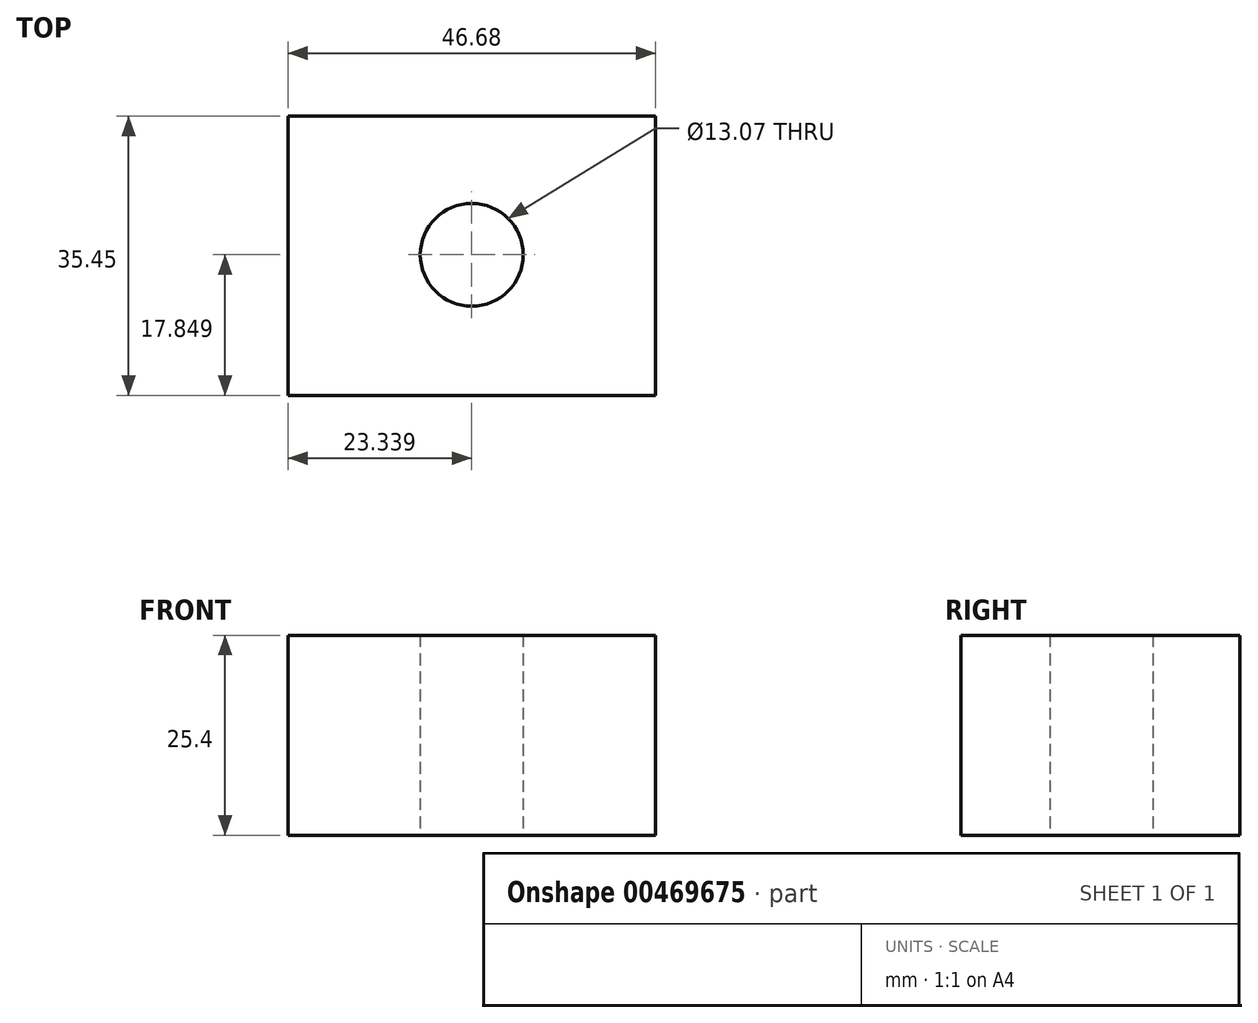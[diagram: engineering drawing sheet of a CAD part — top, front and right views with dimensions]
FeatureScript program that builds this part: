
annotation { "Feature Type Name" : "Feature", "Feature Type Description" : "" }
export const myFeature = defineFeature(function(context is Context, id is Id, definition is map)
    precondition{}
    {
        {
            var Q0;
            Q0=qCreatedBy(makeId("Top.planeOp"),FACE);
            var sketch = newSketch(context, id + "F0", { "sketchPlane" : qUnion([Q0])});
            skLineSegment(sketch, "E0.bottom", {"start": v(0, 0) * mm, "end": v(46.68, 0) * mm});
            skLineSegment(sketch, "E0.top", {"start": v(0, -35.45) * mm, "end": v(46.68, -35.45) * mm});
            skLineSegment(sketch, "E0.left", {"start": v(0, 0) * mm, "end": v(0, -35.45) * mm});
            skLineSegment(sketch, "E0.right", {"start": v(46.68, 0) * mm, "end": v(46.68, -35.45) * mm});
            skCircle(sketch, "E1", {"center": v(23.34, -17.6) * mm, "radius": 6.53 * mm});
            skPoint(sketch, "E1.centerSnap0", {"position": v(23.34, -35.45) * mm});
            skSolve(sketch);
        }
        {
            var Q0;
            Q0=makeQuery(id+"F0.imprint","IMPRINT",FACE,{"disambiguationData":[TD([[makeQuery(id+"F0.imprint","IMPRINT",EDGE,{"derivedFrom":sQuery(id+"F0.wireOp",EDGE,"E0.bottom")}),-1.0]])]});
            extrude(context, id + "F1", {"entities" : qUnion([Q0]), "depth" : 25.4 * mm});
        }
    });
